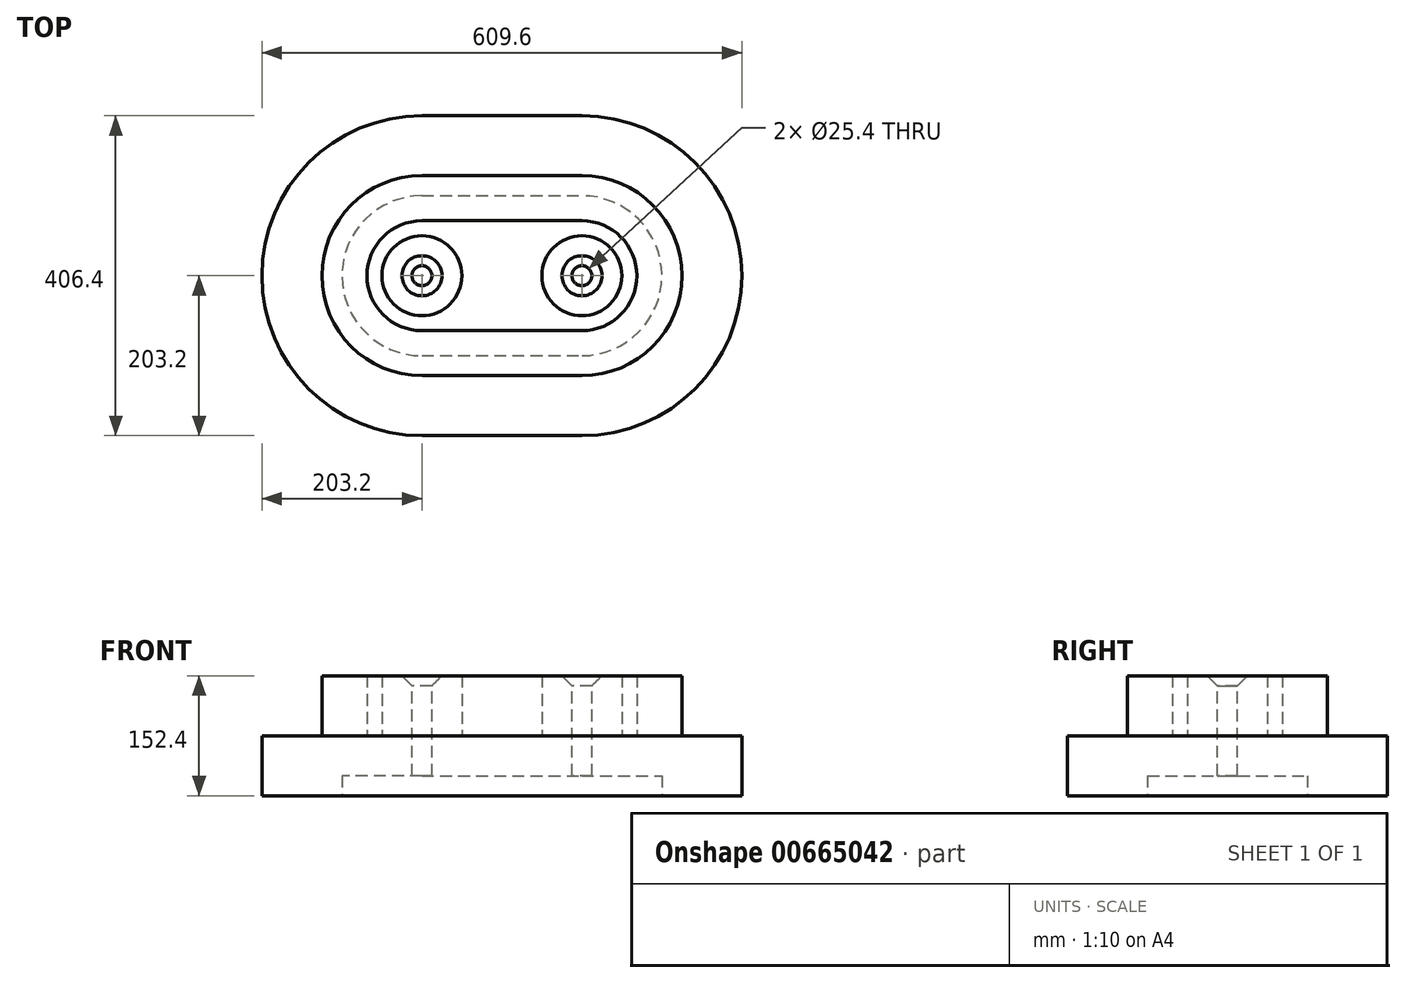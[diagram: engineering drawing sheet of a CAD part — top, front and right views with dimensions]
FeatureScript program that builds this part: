
annotation { "Feature Type Name" : "Feature", "Feature Type Description" : "" }
export const myFeature = defineFeature(function(context is Context, id is Id, definition is map)
    precondition{}
    {
        {
            var Q0;
            Q0=qCreatedBy(makeId("Top.planeOp"),FACE);
            var sketch = newSketch(context, id + "F0", { "sketchPlane" : qUnion([Q0])});
            skLineSegment(sketch, "E0", {"start": v(0, 0) * mm, "end": v(0, 0) * mm});
            skLineSegment(sketch, "E1", {"start": v(203.2, -203.2) * mm, "end": v(406.4, -203.2) * mm});
            skLineSegment(sketch, "E2", {"start": v(609.6, 0) * mm, "end": v(609.6, 0) * mm});
            skLineSegment(sketch, "E3", {"start": v(406.4, 203.2) * mm, "end": v(203.2, 203.2) * mm});
            skPoint(sketch, "E4.visualSharp", {"position": v(0, 203.2) * mm});
            skArc(sketch, "E4.filletArc", {"start": v(203.2, 203.2) * mm, "mid": v(59.52, 143.68) * mm, "end": v(0, 0) * mm});
            skPoint(sketch, "E5.visualSharp", {"position": v(0, -203.2) * mm});
            skArc(sketch, "E5.filletArc", {"start": v(0, 0) * mm, "mid": v(59.52, -143.68) * mm, "end": v(203.2, -203.2) * mm});
            skPoint(sketch, "E6.visualSharp", {"position": v(609.6, -203.2) * mm});
            skArc(sketch, "E6.filletArc", {"start": v(406.4, -203.2) * mm, "mid": v(550.08, -143.68) * mm, "end": v(609.6, 0) * mm});
            skPoint(sketch, "E7.visualSharp", {"position": v(609.6, 203.2) * mm});
            skArc(sketch, "E7.filletArc", {"start": v(609.6, 0) * mm, "mid": v(550.08, 143.68) * mm, "end": v(406.4, 203.2) * mm});
            skLineSegment(sketch, "E8", {"start": v(533.4, 0) * mm, "end": v(533.4, 0) * mm});
            skLineSegment(sketch, "E9", {"start": v(203.2, -127) * mm, "end": v(406.4, -127) * mm});
            skPoint(sketch, "E10.visualSharp", {"position": v(76.2, 127) * mm});
            skLineSegment(sketch, "E11", {"start": v(76.2, 0) * mm, "end": v(76.2, 0) * mm});
            skLineSegment(sketch, "E12", {"start": v(203.2, 127) * mm, "end": v(406.4, 127) * mm});
            skArc(sketch, "E13.filletArc", {"start": v(203.2, 127) * mm, "mid": v(113.4, 89.8) * mm, "end": v(76.2, 0) * mm});
            skPoint(sketch, "E14.visualSharp", {"position": v(76.2, -127) * mm});
            skArc(sketch, "E14.filletArc", {"start": v(76.2, 0) * mm, "mid": v(113.4, -89.8) * mm, "end": v(203.2, -127) * mm});
            skPoint(sketch, "E15.visualSharp", {"position": v(533.4, -127) * mm});
            skArc(sketch, "E15.filletArc", {"start": v(406.4, -127) * mm, "mid": v(496.2, -89.8) * mm, "end": v(533.4, 0) * mm});
            skPoint(sketch, "E16.visualSharp", {"position": v(533.4, 127) * mm});
            skArc(sketch, "E16.filletArc", {"start": v(533.4, 0) * mm, "mid": v(496.2, 89.8) * mm, "end": v(406.4, 127) * mm});
            skLineSegment(sketch, "E17", {"start": v(133.35, 0) * mm, "end": v(133.35, 0) * mm});
            skLineSegment(sketch, "E18", {"start": v(476.25, 0) * mm, "end": v(476.25, 0) * mm});
            skLineSegment(sketch, "E19", {"start": v(406.4, -69.85) * mm, "end": v(203.2, -69.85) * mm});
            skLineSegment(sketch, "E20", {"start": v(406.4, 69.85) * mm, "end": v(203.2, 69.85) * mm});
            skPoint(sketch, "E21.visualSharp", {"position": v(133.35, 69.85) * mm});
            skArc(sketch, "E21.filletArc", {"start": v(203.2, 69.85) * mm, "mid": v(153.8, 49.4) * mm, "end": v(133.35, 0) * mm});
            skPoint(sketch, "E22.visualSharp", {"position": v(133.35, -69.85) * mm});
            skArc(sketch, "E22.filletArc", {"start": v(133.35, 0) * mm, "mid": v(153.8, -49.4) * mm, "end": v(203.2, -69.85) * mm});
            skPoint(sketch, "E23.visualSharp", {"position": v(476.25, -69.85) * mm});
            skArc(sketch, "E23.filletArc", {"start": v(406.4, -69.85) * mm, "mid": v(455.8, -49.4) * mm, "end": v(476.25, 0) * mm});
            skPoint(sketch, "E24.visualSharp", {"position": v(476.25, 69.85) * mm});
            skArc(sketch, "E24.filletArc", {"start": v(476.25, 0) * mm, "mid": v(455.8, 49.4) * mm, "end": v(406.4, 69.85) * mm});
            skLineSegment(sketch, "E25", {"start": v(101.6, 0) * mm, "end": v(101.6, 0) * mm});
            skLineSegment(sketch, "E26", {"start": v(508, 0) * mm, "end": v(508, 0) * mm});
            skPoint(sketch, "E27.visualSharp", {"position": v(101.6, 101.6) * mm});
            skPoint(sketch, "E28.visualSharp", {"position": v(101.6, -101.6) * mm});
            skPoint(sketch, "E29.visualSharp", {"position": v(508, -101.6) * mm});
            skPoint(sketch, "E30.visualSharp", {"position": v(508, 101.6) * mm});
            skCircle(sketch, "E31", {"center": v(203.2, 0) * mm, "radius": 50.8 * mm});
            skCircle(sketch, "E32", {"center": v(406.4, 0) * mm, "radius": 50.8 * mm});
            skCircle(sketch, "E33", {"center": v(203.2, 0) * mm, "radius": 12.7 * mm});
            skCircle(sketch, "E34", {"center": v(406.4, 0) * mm, "radius": 12.7 * mm});
            skLineSegment(sketch, "E35", {"start": v(203.2, -101.6) * mm, "end": v(406.4, -101.6) * mm});
            skLineSegment(sketch, "E36", {"start": v(203.2, 101.6) * mm, "end": v(406.4, 101.6) * mm});
            skArc(sketch, "E37.filletArc", {"start": v(508, 0) * mm, "mid": v(478.24, 71.84) * mm, "end": v(406.4, 101.6) * mm});
            skArc(sketch, "E38.filletArc", {"start": v(406.4, -101.6) * mm, "mid": v(478.24, -71.84) * mm, "end": v(508, 0) * mm});
            skArc(sketch, "E39.filletArc", {"start": v(101.6, 0) * mm, "mid": v(131.36, -71.84) * mm, "end": v(203.2, -101.6) * mm});
            skArc(sketch, "E40.filletArc", {"start": v(203.2, 101.6) * mm, "mid": v(131.36, 71.84) * mm, "end": v(101.6, 0) * mm});
            skSolve(sketch);
        }
        {
            var Q0;
            Q0 = qSketchRegion(id + "F0", true);
            var Q1;
            Q1=makeQuery(id+"F0.imprint","IMPRINT",FACE,{"disambiguationData":[TD([[makeQuery(id+"F0.imprint","IMPRINT",EDGE,{"derivedFrom":sQuery(id+"F0.wireOp",EDGE,"E9")}),1.0]])]});
            var Q2;
            Q2=makeQuery(id+"F0.imprint","IMPRINT",FACE,{"disambiguationData":[TD([[makeQuery(id+"F0.imprint","IMPRINT",EDGE,{"derivedFrom":sQuery(id+"F0.wireOp",EDGE,"E19")}),1.0]])]});
            var Q3;
            Q3=makeQuery(id+"F0.imprint","IMPRINT",FACE,{"disambiguationData":[TD([[makeQuery(id+"F0.imprint","IMPRINT",EDGE,{"derivedFrom":sQuery(id+"F0.wireOp",EDGE,"E19")}),-1.0]])]});
            var Q4;
            Q4=makeQuery(id+"F0.imprint","IMPRINT",FACE,{"disambiguationData":[TD([[makeQuery(id+"F0.imprint","IMPRINT",EDGE,{"derivedFrom":sQuery(id+"F0.wireOp",EDGE,"E32")}),1.0]])]});
            var Q5;
            Q5=makeQuery(id+"F0.imprint","IMPRINT",FACE,{"disambiguationData":[TD([[makeQuery(id+"F0.imprint","IMPRINT",EDGE,{"derivedFrom":sQuery(id+"F0.wireOp",EDGE,"CgRk99A4-T53W-yxqx-XKzd-50J34fkBod5a")}),1.0]])]});
            var Q6;
            Q6=makeQuery(id+"F0.imprint","IMPRINT",FACE,{"disambiguationData":[TD([[makeQuery(id+"F0.imprint","IMPRINT",EDGE,{"derivedFrom":sQuery(id+"F0.wireOp",EDGE,"E31")}),1.0]])]});
            var Q7;
            Q7=makeQuery(id+"F0.imprint","IMPRINT",FACE,{"disambiguationData":[TD([[makeQuery(id+"F0.imprint","IMPRINT",EDGE,{"derivedFrom":sQuery(id+"F0.wireOp",EDGE,"umZkawGg-T6X3-ms80-9Hbh-iHzIvR3WeKTw")}),1.0]])]});
            var Q8;
            Q8=makeQuery(id+"F0.imprint","IMPRINT",FACE,{"disambiguationData":[TD([[makeQuery(id+"F0.imprint","IMPRINT",EDGE,{"derivedFrom":sQuery(id+"F0.wireOp",EDGE,"kCH5ibPO-ePG3-AIAQ-eX6U-32CSvXfOpD0n")}),1.0]])]});
            var Q9;
            Q9=makeQuery(id+"F0.imprint","IMPRINT",FACE,{"disambiguationData":[TD([[makeQuery(id+"F0.imprint","IMPRINT",EDGE,{"derivedFrom":sQuery(id+"F0.wireOp",EDGE,"WY7s3egS-l3Ey-XEGX-0a6X-R2HiGAVVREF3")}),1.0]])]});
            extrude(context, id + "F1", {"entities" : qUnion([Q0, Q1, Q2, Q3, Q4, Q5, Q6, Q7, Q8, Q9]), "depth" : 76.2 * mm, "offsetDistance" : 25.4 * mm});
        }
        {
            var Q0;
            Q0=makeQuery(id+"F0.imprint","IMPRINT",FACE,{"disambiguationData":[TD([[makeQuery(id+"F0.imprint","IMPRINT",EDGE,{"derivedFrom":sQuery(id+"F0.wireOp",EDGE,"E9")}),1.0]])]});
            extrude(context, id + "F2", {"entities" : qUnion([Q0]), "operationType" : NewBodyOperationType.ADD, "depth" : 152.4 * mm, "offsetDistance" : 25.4 * mm});
        }
        {
            var Q0;
            Q0=makeQuery(id+"F0.imprint","IMPRINT",FACE,{"disambiguationData":[TD([[makeQuery(id+"F0.imprint","IMPRINT",EDGE,{"derivedFrom":sQuery(id+"F0.wireOp",EDGE,"E31")}),1.0]])]});
            var Q1;
            Q1=makeQuery(id+"F0.imprint","IMPRINT",FACE,{"disambiguationData":[TD([[makeQuery(id+"F0.imprint","IMPRINT",EDGE,{"derivedFrom":sQuery(id+"F0.wireOp",EDGE,"E32")}),1.0]])]});
            var Q2;
            Q2=makeQuery(id+"F0.imprint","IMPRINT",FACE,{"disambiguationData":[TD([[makeQuery(id+"F0.imprint","IMPRINT",EDGE,{"derivedFrom":sQuery(id+"F0.wireOp",EDGE,"E33")}),1.0]])]});
            var Q3;
            Q3=makeQuery(id+"F0.imprint","IMPRINT",FACE,{"disambiguationData":[TD([[makeQuery(id+"F0.imprint","IMPRINT",EDGE,{"derivedFrom":sQuery(id+"F0.wireOp",EDGE,"E34")}),1.0]])]});
            extrude(context, id + "F3", {"entities" : qUnion([Q0, Q1, Q2, Q3]), "operationType" : NewBodyOperationType.ADD, "depth" : 152.4 * mm, "offsetDistance" : 25.4 * mm});
        }
        {
            var Q0;
            Q0=makeQuery(id+"F0.imprint","IMPRINT",FACE,{"disambiguationData":[TD([[makeQuery(id+"F0.imprint","IMPRINT",EDGE,{"derivedFrom":sQuery(id+"F0.wireOp",EDGE,"E19")}),1.0]])]});
            var Q1;
            Q1=makeQuery(id+"F0.imprint","IMPRINT",FACE,{"disambiguationData":[TD([[makeQuery(id+"F0.imprint","IMPRINT",EDGE,{"derivedFrom":sQuery(id+"F0.wireOp",EDGE,"E19")}),-1.0]])]});
            var Q2;
            Q2=makeQuery(id+"F0.imprint","IMPRINT",FACE,{"disambiguationData":[TD([[makeQuery(id+"F0.imprint","IMPRINT",EDGE,{"derivedFrom":sQuery(id+"F0.wireOp",EDGE,"E31")}),1.0]])]});
            var Q3;
            Q3=makeQuery(id+"F0.imprint","IMPRINT",FACE,{"disambiguationData":[TD([[makeQuery(id+"F0.imprint","IMPRINT",EDGE,{"derivedFrom":sQuery(id+"F0.wireOp",EDGE,"E32")}),1.0]])]});
            extrude(context, id + "F4", {"entities" : qUnion([Q0, Q1, Q2, Q3]), "operationType" : NewBodyOperationType.REMOVE, "depth" : 25.4 * mm, "offsetDistance" : 25.4 * mm});
        }
        {
            var Q0;
            Q0=makeQuery(id+"F0.imprint","IMPRINT",FACE,{"disambiguationData":[TD([[makeQuery(id+"F0.imprint","IMPRINT",EDGE,{"derivedFrom":sQuery(id+"F0.wireOp",EDGE,"E19")}),1.0]])]});
            extrude(context, id + "F5", {"entities" : qUnion([Q0]), "operationType" : NewBodyOperationType.ADD, "depth" : 152.4 * mm, "offsetDistance" : 25.4 * mm, "hasSecondDirection" : true, "secondDirectionOppositeDirection" : false, "secondDirectionDepth" : 25.4 * mm});
        }
        {
            var Q0;
            Q0=makeQuery(id+"F3.opExtrude","CAP_FACE",FACE,{"disambiguationData":[OSD([sQuery(id+"F0.wireOp",EDGE,"E31")])],"isStart":false});
            var sketch = newSketch(context, id + "F6", { "sketchPlane" : qUnion([Q0])});
            skLineSegment(sketch, "E41", {"start": v(0, 0) * mm, "end": v(203.2, 0) * mm});
            skLineSegment(sketch, "E42", {"start": v(203.2, 0) * mm, "end": v(406.4, 0) * mm});
            skSolve(sketch);
        }
        {
            var Q0;
            Q0=sQuery(id+"F6.wireOp",VERTEX,"E41.end");
            var Q1;
            Q1=sQuery(id+"F6.wireOp",VERTEX,"E42.end");
            var Q2;
            Q2=makeQuery(id+"F1.opExtrude","SWEPT_BODY",BODY,{"disambiguationData":[OSD([sQuery(id+"F0.wireOp",EDGE,"E1"),sQuery(id+"F0.wireOp",EDGE,"E3"),sQuery(id+"F0.wireOp",EDGE,"E4.filletArc"),sQuery(id+"F0.wireOp",EDGE,"E5.filletArc"),sQuery(id+"F0.wireOp",EDGE,"E6.filletArc"),sQuery(id+"F0.wireOp",EDGE,"E7.filletArc"),sQuery(id+"F0.wireOp",EDGE,"E33"),sQuery(id+"F0.wireOp",EDGE,"E34")])]});
            hole(context, id + "F7", {"style" : HoleStyle.C_SINK, "endStyle" : HoleEndStyle.THROUGH, "holeDiameter" : 25.4 * mm, "cSinkDiameter" : 50.8 * mm, "cSinkAngle" : 90 * degree, "majorDiameter" : 6.35 * mm, "isTappedThrough" : true, "tappedDepth" : 12.7 * mm, "tapClearance" : 3, "locations" : qUnion([Q0, Q1]), "scope" : qUnion([Q2])});
        }
    });
